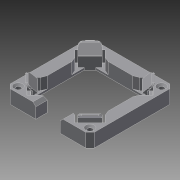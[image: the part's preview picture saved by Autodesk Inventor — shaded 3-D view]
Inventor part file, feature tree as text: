
AUTODESK INVENTOR PART (.ipt)
format: ipt  version: 2021.3 (Build 253353000, 353)  size: 386,560 bytes
history: native  units: mm
features: reference x13, other x9, sketch x6, extrude x5, chamfer x4, fillet x3, hole x2, pattern_circular x1, projected_geometry x1
ambient origin geometry x8: Origin, YZ Plane, XZ Plane, XY Plane, X Axis, Y Axis, Z Axis, Center Point
bodies: Body1 (feature_tree)
feature tree (44):
  other  "Твердое тело1"
  other  "РабПлоскость1"
  extrude  "Выдавливание1"  Depth=0.2mm
  other  "РабПлоскость2"
  extrude  "Выдавливание2"  Depth=4.0mm
  chamfer  "Фаска3"  Distance=4.0mm
  extrude  "Выдавливание3"  Depth=4.0mm
  fillet  "Сопряжение4"  Radius=4.0mm
  fillet  "Сопряжение2"  Radius=4.0mm
  fillet  "Сопряжение5"  Radius=4.0mm
  pattern_circular  "Круговой массив2"  [2 undecoded]
  chamfer  "Фаска4"  Distance=4.0mm
  hole  "Отверстие1"  [1 undecoded]
  chamfer  "Фаска1"  Distance=8.0mm
  extrude  "Выдавливание4"  Depth=3.0mm
  chamfer  "Фаска2"  Distance=5.656854mm
  extrude  "Выдавливание5"  Depth=6.0mm
  hole  "Отверстие2"  [1 undecoded]
  sketch  "Эскиз1"
  reference  "Ссылка1"
  reference  "Ссылка2"
  reference  "Ссылка3"
  reference  "Ссылка4"
  reference  "Ссылка5"
  reference  "Ссылка6"
  reference  "Ссылка7"
  reference  "Ссылка8"
  reference  "Ссылка9"
  sketch  "Эскиз3"
  reference  "Ссылка10"
  reference  "Ссылка11"
  reference  "Ссылка12"
  sketch  "Эскиз5"
  sketch  "Эскиз6"
  reference  "Ссылка13"
  sketch  "Эскиз7"
  projected_geometry  "Спроецированная петля1"
  sketch  "Эскиз8"
  parser-record x1  (decoder bookkeeping rows leaked as tree rows — omitted from the tree; the rows remain in map.json)
  other  "Nema17.iam"
  other  "Pumpshare:1"
  other  "Middle:1"
  other  "Top:1"
  other  "Bottom:1"
note: 4 required parameter values undecoded (feature->parameter linkage not recoverable at this tier; creation-order binding heuristic only, values carry confidence <= 0.55)
note: 1 file-system path scrubbed to <path> (originals preserved in map.json)
